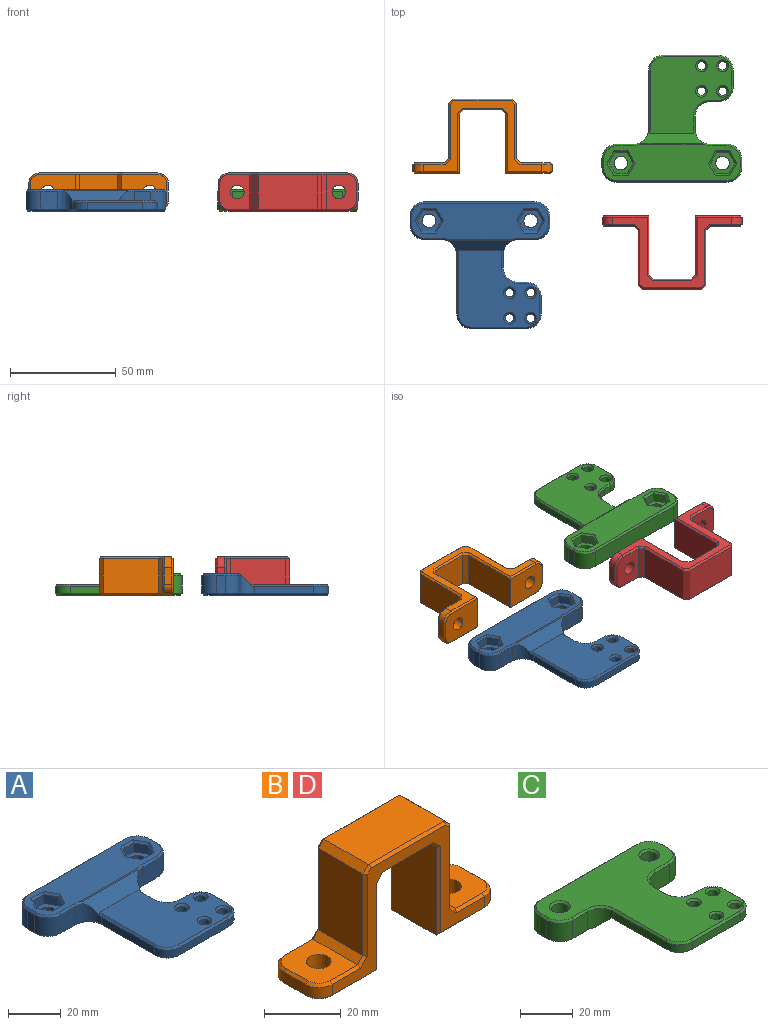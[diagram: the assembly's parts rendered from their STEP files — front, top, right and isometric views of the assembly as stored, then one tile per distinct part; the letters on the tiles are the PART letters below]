
ASSEMBLY  parts=4 mates=3
PART A: 109 faces, bbox 66x60x10 mm
  f0: plane 8.4x8mm, normal (0,-1,0), area 67.2mm2, adj f34,f35,f63,f89
  f1: plane 11.55x10mm, normal (0,0,1), area 54.4mm2, adj f18,f25,f26,f27,f28,f29,f30
  f2: plane 38.66x36.2mm, normal (0,0,1), area 995.8mm2, adj f43,f44,f45,f46,f47,f48,f49,f50
  f3: plane 11.55x10mm, normal (0,0,1), area 54.4mm2, adj f16,f20,f21,f22,f23,f24,f31
  f4: plane 28x3.4mm, normal (-1,0,0), area 95.2mm2, adj f35,f39,f53,f85
  f5: plane 26x3.4mm, normal (0,-1,0), area 88.4mm2, adj f39,f41,f51,f84
  f6: plane 8x3.4mm, normal (1,0,0), area 27.2mm2, adj f41,f42,f49,f88
  f7: plane 4x3.4mm, normal (0,1,0), area 13.6mm2, adj f40,f42,f47,f92
  f8: plane 6x3.4mm, normal (1,0,0), area 20.4mm2, adj f36,f40,f45,f96
  f9: plane 8.4x8mm, normal (0,-1,0), area 67.2mm2, adj f36,f37,f70,f100
  f10: plane 8.4x4mm, normal (1,0,0), area 33.6mm2, adj f37,f38,f66,f101
  f11: plane 52x8.4mm, normal (0,1,0), area 436.8mm2, adj f33,f38,f62,f97
  f12: cylinder r=2mm len=4mm, axis (0,0,1), area 42.7mm2, adj f58,f108
  f13: cylinder r=2mm len=4mm, axis (0,0,1), area 42.7mm2, adj f56,f107
  f14: cylinder r=2mm len=4mm, axis (0,0,1), area 42.7mm2, adj f57,f106
  f15: cylinder r=2mm len=4mm, axis (0,0,1), area 42.7mm2, adj f55,f105
  f16: cylinder r=3.2mm len=6.4mm, axis (0,0,1), area 84.4mm2, adj f3,f103
  f17: plane 8.4x4mm, normal (-1,0,0), area 33.6mm2, adj f33,f34,f59,f93
  f18: cylinder r=3.2mm len=6.4mm, axis (0,0,1), area 84.4mm2, adj f1,f104
  f19: plane 64.4x58.4mm, normal (0,0,-1), area 2062.5mm2, adj f83,f84,f85,f86,f87,f88,f89,f90
  f20: plane 5.77x4.2mm, normal (0,-1,0), area 24.2mm2, adj f3,f21,f31,f75
  f21: plane 5x4.2mm, normal (-0.87,-0.5,0), area 24.2mm2, adj f3,f20,f22,f76
  f22: plane 5x4.2mm, normal (-0.87,0.5,0), area 24.2mm2, adj f3,f21,f23,f74
  f23: plane 5.77x4.2mm, normal (0,1,0), area 24.2mm2, adj f3,f22,f24,f72
  f24: plane 5x4.2mm, normal (0.87,0.5,0), area 24.2mm2, adj f3,f23,f31,f71
  f25: plane 5.77x4.2mm, normal (0,-1,0), area 24.2mm2, adj f1,f26,f30,f81
  f26: plane 5x4.2mm, normal (-0.87,-0.5,0), area 24.2mm2, adj f1,f25,f27,f82
  f27: plane 5x4.2mm, normal (-0.87,0.5,0), area 24.2mm2, adj f1,f26,f28,f80
  f28: plane 5.77x4.2mm, normal (0,1,0), area 24.2mm2, adj f1,f27,f29,f78
  f29: plane 5x4.2mm, normal (0.87,0.5,0), area 24.2mm2, adj f1,f28,f30,f77
  f30: plane 5x4.2mm, normal (0.87,-0.5,0), area 24.2mm2, adj f1,f25,f29,f79
  f31: plane 5x4.2mm, normal (0.87,-0.5,0), area 24.2mm2, adj f3,f20,f24,f73
  f32: plane 64.4x16.87mm, normal (0,0,1), area 805.3mm2, adj f59,f60,f61,f62,f63,f64,f65,f66
  f33: cylinder r=7mm len=8.4mm, axis (0,0,1), area 92.4mm2, adj f11,f17,f60,f95
  f34: cylinder r=7mm len=8.4mm, axis (0,0,1), area 92.4mm2, adj f0,f17,f61,f91
  f35: cylinder r=7mm len=8.4mm, axis (0,0,-1), area 72.1mm2, adj f0,f4,f43,f54,f65,f87
  f36: cylinder r=7mm len=8.4mm, axis (0,0,1), area 72.1mm2, adj f8,f9,f43,f44,f69,f98
  f37: cylinder r=7mm len=8.4mm, axis (0,0,-1), area 92.4mm2, adj f9,f10,f68,f102
  f38: cylinder r=7mm len=8.4mm, axis (0,0,-1), area 92.4mm2, adj f10,f11,f64,f99
  f39: cylinder r=7mm len=7mm, axis (0,0,1), area 37.4mm2, adj f4,f5,f52,f83
  f40: cylinder r=7mm len=7mm, axis (0,0,-1), area 37.4mm2, adj f7,f8,f46,f94
  f41: cylinder r=7mm len=7mm, axis (0,0,1), area 37.4mm2, adj f5,f6,f50,f86
  f42: cylinder r=7mm len=7mm, axis (0,0,-1), area 37.4mm2, adj f6,f7,f48,f90
  f43: plane 29.5x5.57mm, normal (0,-0.71,0.71), area 173.4mm2, adj f2,f35,f36,f44,f54,f65,f67,f69
  f44: cone r=7.8mm half-angle=45deg, axis (0,0,1), area 1.8mm2, adj f2,f36,f43,f45
  f45: plane 6x0.8mm, normal (0.71,0,0.71), area 6.8mm2, adj f2,f8,f44,f46
  f46: cone r=7.8mm half-angle=45deg, axis (0,0,1), area 13.2mm2, adj f2,f40,f45,f47
  f47: plane 4x0.8mm, normal (0,0.71,0.71), area 4.5mm2, adj f2,f7,f46,f48
  f48: cone r=6.2mm half-angle=45deg, axis (0,0,-1), area 11.7mm2, adj f2,f42,f47,f49
  f49: plane 8x0.8mm, normal (0.71,0,0.71), area 9.1mm2, adj f2,f6,f48,f50
  f50: cone r=6.2mm half-angle=45deg, axis (0,0,-1), area 11.7mm2, adj f2,f41,f49,f51
  f51: plane 26x0.8mm, normal (0,-0.71,0.71), area 29.4mm2, adj f2,f5,f50,f52
  f52: cone r=6.2mm half-angle=45deg, axis (0,0,-1), area 11.7mm2, adj f2,f39,f51,f53
  f53: plane 28x0.8mm, normal (-0.71,0,0.71), area 31.7mm2, adj f2,f4,f52,f54
  f54: cone r=7.8mm half-angle=45deg, axis (0,0,1), area 1.8mm2, adj f2,f35,f43,f53
  f55: cone r=2.8mm half-angle=45deg, axis (0,0,1), area 17.1mm2, adj f2,f15
  f56: cone r=2.8mm half-angle=45deg, axis (0,0,1), area 17.1mm2, adj f2,f13
  f57: cone r=2.8mm half-angle=45deg, axis (0,0,1), area 17.1mm2, adj f2,f14
  f58: cone r=2.8mm half-angle=45deg, axis (0,0,1), area 17.1mm2, adj f2,f12
  f59: plane 4x0.8mm, normal (-0.71,0,0.71), area 4.5mm2, adj f17,f32,f60,f61
  f60: cone r=6.2mm half-angle=45deg, axis (0,0,-1), area 11.7mm2, adj f32,f33,f59,f62
  f61: cone r=6.2mm half-angle=45deg, axis (0,0,-1), area 11.7mm2, adj f32,f34,f59,f63
  f62: plane 52x0.8mm, normal (0,0.71,0.71), area 58.8mm2, adj f11,f32,f60,f64
  f63: plane 8x0.8mm, normal (0,-0.71,0.71), area 9.1mm2, adj f0,f32,f61,f65
  f64: cone r=6.2mm half-angle=45deg, axis (0,0,-1), area 11.7mm2, adj f32,f38,f62,f66
  f65: cone r=7.8mm half-angle=45deg, axis (0,0,1), area 3.8mm2, adj f32,f35,f43,f63,f67
  f66: plane 4x0.8mm, normal (0.71,0,0.71), area 4.5mm2, adj f10,f32,f64,f68
  f67: plane 30.67x0.57mm, normal (0,-0.38,0.92), area 18.3mm2, adj f32,f43,f65,f69
  f68: cone r=6.2mm half-angle=45deg, axis (0,0,-1), area 11.7mm2, adj f32,f37,f66,f70
  f69: cone r=7.8mm half-angle=45deg, axis (0,0,1), area 3.8mm2, adj f32,f36,f43,f67,f70
  f70: plane 8x0.8mm, normal (0,-0.71,0.71), area 9.1mm2, adj f9,f32,f68,f69
  f71: plane 5.8x3.81mm, normal (0.61,0.35,0.71), area 7.1mm2, adj f24,f32,f72,f73
  f72: plane 6.7x0.8mm, normal (0,0.71,0.71), area 7.1mm2, adj f23,f32,f71,f74
  f73: plane 5.8x3.81mm, normal (0.61,-0.35,0.71), area 7.1mm2, adj f31,f32,f71,f75
  f74: plane 5.8x3.81mm, normal (-0.61,0.35,0.71), area 7.1mm2, adj f22,f32,f72,f76
  f75: plane 6.7x0.8mm, normal (0,-0.71,0.71), area 7.1mm2, adj f20,f32,f73,f76
  f76: plane 5.8x3.81mm, normal (-0.61,-0.35,0.71), area 7.1mm2, adj f21,f32,f74,f75
  f77: plane 5.8x3.81mm, normal (0.61,0.35,0.71), area 7.1mm2, adj f29,f32,f78,f79
  f78: plane 6.7x0.8mm, normal (0,0.71,0.71), area 7.1mm2, adj f28,f32,f77,f80
  f79: plane 5.8x3.81mm, normal (0.61,-0.35,0.71), area 7.1mm2, adj f30,f32,f77,f81
  f80: plane 5.8x3.81mm, normal (-0.61,0.35,0.71), area 7.1mm2, adj f27,f32,f78,f82
  f81: plane 6.7x0.8mm, normal (0,-0.71,0.71), area 7.1mm2, adj f25,f32,f79,f82
  f82: plane 5.8x3.81mm, normal (-0.61,-0.35,0.71), area 7.1mm2, adj f26,f32,f80,f81
  f83: cone r=6.2mm half-angle=45deg, axis (0,0,1), area 11.7mm2, adj f19,f39,f84,f85
  f84: plane 26x0.8mm, normal (0,-0.71,-0.71), area 29.4mm2, adj f5,f19,f83,f86
  f85: plane 28x0.8mm, normal (-0.71,0,-0.71), area 31.7mm2, adj f4,f19,f83,f87
  f86: cone r=6.2mm half-angle=45deg, axis (0,0,1), area 11.7mm2, adj f19,f41,f84,f88
  f87: cone r=7.8mm half-angle=45deg, axis (0,0,-1), area 13.2mm2, adj f19,f35,f85,f89
  f88: plane 8x0.8mm, normal (0.71,0,-0.71), area 9.1mm2, adj f6,f19,f86,f90
  f89: plane 8x0.8mm, normal (0,-0.71,-0.71), area 9.1mm2, adj f0,f19,f87,f91
  f90: cone r=6.2mm half-angle=45deg, axis (0,0,1), area 11.7mm2, adj f19,f42,f88,f92
  f91: cone r=6.2mm half-angle=45deg, axis (0,0,1), area 11.7mm2, adj f19,f34,f89,f93
  f92: plane 4x0.8mm, normal (0,0.71,-0.71), area 4.5mm2, adj f7,f19,f90,f94
  f93: plane 4x0.8mm, normal (-0.71,0,-0.71), area 4.5mm2, adj f17,f19,f91,f95
  f94: cone r=7.8mm half-angle=45deg, axis (0,0,-1), area 13.2mm2, adj f19,f40,f92,f96
  f95: cone r=6.2mm half-angle=45deg, axis (0,0,1), area 11.7mm2, adj f19,f33,f93,f97
  f96: plane 6x0.8mm, normal (0.71,0,-0.71), area 6.8mm2, adj f8,f19,f94,f98
  f97: plane 52x0.8mm, normal (0,0.71,-0.71), area 58.8mm2, adj f11,f19,f95,f99
  f98: cone r=7.8mm half-angle=45deg, axis (0,0,-1), area 13.2mm2, adj f19,f36,f96,f100
  f99: cone r=6.2mm half-angle=45deg, axis (0,0,1), area 11.7mm2, adj f19,f38,f97,f101
  f100: plane 8x0.8mm, normal (0,-0.71,-0.71), area 9.1mm2, adj f9,f19,f98,f102
  f101: plane 4x0.8mm, normal (0.71,0,-0.71), area 4.5mm2, adj f10,f19,f99,f102
  f102: cone r=6.2mm half-angle=45deg, axis (0,0,1), area 11.7mm2, adj f19,f37,f100,f101
  f103: cone r=3.2mm half-angle=45deg, axis (0,0,-1), area 25.6mm2, adj f16,f19
  f104: cone r=3.2mm half-angle=45deg, axis (0,0,-1), area 25.6mm2, adj f18,f19
  f105: cone r=2mm half-angle=45deg, axis (0,0,-1), area 17.1mm2, adj f15,f19
  f106: cone r=2mm half-angle=45deg, axis (0,0,-1), area 17.1mm2, adj f14,f19
  f107: cone r=2mm half-angle=45deg, axis (0,0,-1), area 17.1mm2, adj f13,f19
  f108: cone r=2mm half-angle=45deg, axis (0,0,-1), area 17.1mm2, adj f12,f19
PART B: 70 faces, bbox 66x18x35 mm
  f0: plane 16.4x14.2mm, normal (0,0,1), area 193.1mm2, adj f5,f21,f26,f27,f28,f29,f30
  f1: plane 56x33.4mm, normal (0,-1,0), area 404.2mm2, adj f16,f18,f30,f32,f34,f36,f38,f40
  f2: plane 28x16.4mm, normal (1,0,0), area 459.2mm2, adj f6,f24,f55,f56
  f3: plane 56x33.4mm, normal (0,1,0), area 404.2mm2, adj f17,f19,f29,f31,f33,f35,f37,f39
  f4: plane 8x3.4mm, normal (-1,0,0), area 27.2mm2, adj f18,f19,f26,f50
  f5: cylinder r=3.2mm len=6.4mm, axis (0,0,1), area 100.5mm2, adj f0,f6
  f6: plane 21.2x16.4mm, normal (0,0,-1), area 307.9mm2, adj f2,f5,f50,f51,f52,f53,f54
  f7: plane 26x16.4mm, normal (-1,0,0), area 426.4mm2, adj f21,f25,f33,f34
  f8: plane 18x16.4mm, normal (0,0,-1), area 295.2mm2, adj f23,f24,f59,f60
  f9: plane 28x16.4mm, normal (-1,0,0), area 459.2mm2, adj f12,f23,f63,f64
  f10: plane 8x3.4mm, normal (1,0,0), area 27.2mm2, adj f16,f17,f49,f69
  f11: cylinder r=3.2mm len=6.4mm, axis (0,0,1), area 100.5mm2, adj f12,f13
  f12: plane 21.2x16.4mm, normal (0,0,-1), area 307.9mm2, adj f9,f11,f65,f66,f67,f68,f69
  f13: plane 16.4x14.2mm, normal (0,0,1), area 193.1mm2, adj f11,f20,f45,f46,f47,f48,f49
  f14: plane 26x16.4mm, normal (1,0,0), area 426.4mm2, adj f20,f22,f41,f42
  f15: plane 28x16.4mm, normal (0,0,1), area 459.2mm2, adj f22,f25,f37,f38
  f16: cylinder r=5mm len=5mm, axis (0,0,1), area 26.7mm2, adj f1,f10,f48,f68
  f17: cylinder r=5mm len=5mm, axis (0,0,-1), area 26.7mm2, adj f3,f10,f47,f67
  f18: cylinder r=5mm len=5mm, axis (0,0,-1), area 26.7mm2, adj f1,f4,f28,f52
  f19: cylinder r=5mm len=5mm, axis (0,0,1), area 26.7mm2, adj f3,f4,f27,f51
  f20: plane 16.4x2mm, normal (0.71,0,0.71), area 46.4mm2, adj f13,f14,f43,f44
  f21: plane 16.4x2mm, normal (-0.71,0,0.71), area 46.4mm2, adj f0,f7,f31,f32
  f22: plane 16.4x2mm, normal (0.71,0,0.71), area 46.4mm2, adj f14,f15,f39,f40
  f23: plane 16.4x2mm, normal (-0.71,0,-0.71), area 46.4mm2, adj f8,f9,f61,f62
  f24: plane 16.4x2mm, normal (0.71,0,-0.71), area 46.4mm2, adj f2,f8,f57,f58
  f25: plane 16.4x2mm, normal (-0.71,0,0.71), area 46.4mm2, adj f7,f15,f35,f36
  f26: plane 8x0.8mm, normal (-0.71,0,0.71), area 9.1mm2, adj f0,f4,f27,f28
  f27: cone r=4.2mm half-angle=45deg, axis (0,0,-1), area 8.2mm2, adj f0,f19,f26,f29
  f28: cone r=4.2mm half-angle=45deg, axis (0,0,-1), area 8.2mm2, adj f0,f18,f26,f30
  f29: plane 10.33x0.8mm, normal (0,0.71,0.71), area 11.5mm2, adj f0,f3,f27,f31
  f30: plane 10.33x0.8mm, normal (0,-0.71,0.71), area 11.5mm2, adj f0,f1,f28,f32
  f31: plane 2.8x2.8mm, normal (-0.5,0.71,0.5), area 3.6mm2, adj f3,f21,f29,f33
  f32: plane 2.8x2.8mm, normal (-0.5,-0.71,0.5), area 3.6mm2, adj f1,f21,f30,f34
  f33: plane 26.33x0.8mm, normal (-0.71,0.71,0), area 29.4mm2, adj f3,f7,f31,f35
  f34: plane 26.33x0.8mm, normal (-0.71,-0.71,0), area 29.4mm2, adj f1,f7,f32,f36
  f35: plane 2.33x2.33mm, normal (-0.5,0.71,0.5), area 2.8mm2, adj f3,f25,f33,f37
  f36: plane 2.33x2.33mm, normal (-0.5,-0.71,0.5), area 2.8mm2, adj f1,f25,f34,f38
  f37: plane 28x0.8mm, normal (0,0.71,0.71), area 31.3mm2, adj f3,f15,f35,f39
  f38: plane 28x0.8mm, normal (0,-0.71,0.71), area 31.3mm2, adj f1,f15,f36,f40
  f39: plane 2.33x2.33mm, normal (0.5,0.71,0.5), area 2.8mm2, adj f3,f22,f37,f41
  f40: plane 2.33x2.33mm, normal (0.5,-0.71,0.5), area 2.8mm2, adj f1,f22,f38,f42
  f41: plane 26.33x0.8mm, normal (0.71,0.71,0), area 29.4mm2, adj f3,f14,f39,f43
  f42: plane 26.33x0.8mm, normal (0.71,-0.71,0), area 29.4mm2, adj f1,f14,f40,f44
  f43: plane 2.8x2.8mm, normal (0.5,0.71,0.5), area 3.6mm2, adj f3,f20,f41,f45
  f44: plane 2.8x2.8mm, normal (0.5,-0.71,0.5), area 3.6mm2, adj f1,f20,f42,f46
  f45: plane 10.33x0.8mm, normal (0,0.71,0.71), area 11.5mm2, adj f3,f13,f43,f47
  f46: plane 10.33x0.8mm, normal (0,-0.71,0.71), area 11.5mm2, adj f1,f13,f44,f48
  f47: cone r=4.2mm half-angle=45deg, axis (0,0,-1), area 8.2mm2, adj f13,f17,f45,f49
  f48: cone r=4.2mm half-angle=45deg, axis (0,0,-1), area 8.2mm2, adj f13,f16,f46,f49
  f49: plane 8x0.8mm, normal (0.71,0,0.71), area 9.1mm2, adj f10,f13,f47,f48
  f50: plane 8x0.8mm, normal (-0.71,0,-0.71), area 9.1mm2, adj f4,f6,f51,f52
  f51: cone r=4.2mm half-angle=45deg, axis (0,0,1), area 8.2mm2, adj f6,f19,f50,f53
  f52: cone r=4.2mm half-angle=45deg, axis (0,0,1), area 8.2mm2, adj f6,f18,f50,f54
  f53: plane 17x0.8mm, normal (0,0.71,-0.71), area 18.8mm2, adj f3,f6,f51,f55
  f54: plane 17x0.8mm, normal (0,-0.71,-0.71), area 18.8mm2, adj f1,f6,f52,f56
  f55: plane 28.33x0.8mm, normal (0.71,0.71,0), area 31.4mm2, adj f2,f3,f53,f57
  f56: plane 28.33x0.8mm, normal (0.71,-0.71,0), area 31.4mm2, adj f1,f2,f54,f58
  f57: plane 2.8x2.8mm, normal (0.5,0.71,-0.5), area 3.6mm2, adj f3,f24,f55,f59
  f58: plane 2.8x2.8mm, normal (0.5,-0.71,-0.5), area 3.6mm2, adj f1,f24,f56,f60
  f59: plane 18.66x0.8mm, normal (0,0.71,-0.71), area 20.7mm2, adj f3,f8,f57,f61
  f60: plane 18.66x0.8mm, normal (0,-0.71,-0.71), area 20.7mm2, adj f1,f8,f58,f62
  f61: plane 2.8x2.8mm, normal (-0.5,0.71,-0.5), area 3.6mm2, adj f3,f23,f59,f63
  f62: plane 2.8x2.8mm, normal (-0.5,-0.71,-0.5), area 3.6mm2, adj f1,f23,f60,f64
  f63: plane 28.33x0.8mm, normal (-0.71,0.71,0), area 31.4mm2, adj f3,f9,f61,f65
  f64: plane 28.33x0.8mm, normal (-0.71,-0.71,0), area 31.4mm2, adj f1,f9,f62,f66
  f65: plane 17x0.8mm, normal (0,0.71,-0.71), area 18.8mm2, adj f3,f12,f63,f67
  f66: plane 17x0.8mm, normal (0,-0.71,-0.71), area 18.8mm2, adj f1,f12,f64,f68
  f67: cone r=4.2mm half-angle=45deg, axis (0,0,1), area 8.2mm2, adj f12,f17,f65,f69
  f68: cone r=4.2mm half-angle=45deg, axis (0,0,1), area 8.2mm2, adj f12,f16,f66,f69
  f69: plane 8x0.8mm, normal (0.71,0,-0.71), area 9.1mm2, adj f10,f12,f67,f68
PART C: 109 faces, bbox 66x60x10 mm
  f0: plane 8.4x8mm, normal (0,-1,0), area 67.2mm2, adj f34,f35,f63,f89
  f1: plane 11.55x10mm, normal (0,0,-1), area 54.4mm2, adj f18,f25,f26,f27,f28,f29,f30
  f2: plane 38.66x36.2mm, normal (0,0,-1), area 995.8mm2, adj f43,f44,f45,f46,f47,f48,f49,f50
  f3: plane 11.55x10mm, normal (0,0,-1), area 54.4mm2, adj f16,f20,f21,f22,f23,f24,f31
  f4: plane 28x3.4mm, normal (-1,0,0), area 95.2mm2, adj f35,f39,f53,f85
  f5: plane 26x3.4mm, normal (0,-1,0), area 88.4mm2, adj f39,f41,f51,f84
  f6: plane 8x3.4mm, normal (1,0,0), area 27.2mm2, adj f41,f42,f49,f88
  f7: plane 4x3.4mm, normal (0,1,0), area 13.6mm2, adj f40,f42,f47,f92
  f8: plane 6x3.4mm, normal (1,0,0), area 20.4mm2, adj f36,f40,f45,f96
  f9: plane 8.4x8mm, normal (0,-1,0), area 67.2mm2, adj f36,f37,f70,f100
  f10: plane 8.4x4mm, normal (1,0,0), area 33.6mm2, adj f37,f38,f66,f101
  f11: plane 52x8.4mm, normal (0,1,0), area 436.8mm2, adj f33,f38,f62,f97
  f12: cylinder r=2mm len=4mm, axis (0,0,-1), area 42.7mm2, adj f58,f108
  f13: cylinder r=2mm len=4mm, axis (0,0,-1), area 42.7mm2, adj f56,f107
  f14: cylinder r=2mm len=4mm, axis (0,0,-1), area 42.7mm2, adj f57,f106
  f15: cylinder r=2mm len=4mm, axis (0,0,-1), area 42.7mm2, adj f55,f105
  f16: cylinder r=3.2mm len=6.4mm, axis (0,0,-1), area 84.4mm2, adj f3,f103
  f17: plane 8.4x4mm, normal (-1,0,0), area 33.6mm2, adj f33,f34,f59,f93
  f18: cylinder r=3.2mm len=6.4mm, axis (0,0,-1), area 84.4mm2, adj f1,f104
  f19: plane 64.4x58.4mm, normal (0,0,1), area 2062.5mm2, adj f83,f84,f85,f86,f87,f88,f89,f90
  f20: plane 5.77x4.2mm, normal (0,-1,0), area 24.2mm2, adj f3,f21,f31,f75
  f21: plane 5x4.2mm, normal (-0.87,-0.5,0), area 24.2mm2, adj f3,f20,f22,f76
  f22: plane 5x4.2mm, normal (-0.87,0.5,0), area 24.2mm2, adj f3,f21,f23,f74
  f23: plane 5.77x4.2mm, normal (0,1,0), area 24.2mm2, adj f3,f22,f24,f72
  f24: plane 5x4.2mm, normal (0.87,0.5,0), area 24.2mm2, adj f3,f23,f31,f71
  f25: plane 5.77x4.2mm, normal (0,-1,0), area 24.2mm2, adj f1,f26,f30,f81
  f26: plane 5x4.2mm, normal (-0.87,-0.5,0), area 24.2mm2, adj f1,f25,f27,f82
  f27: plane 5x4.2mm, normal (-0.87,0.5,0), area 24.2mm2, adj f1,f26,f28,f80
  f28: plane 5.77x4.2mm, normal (0,1,0), area 24.2mm2, adj f1,f27,f29,f78
  f29: plane 5x4.2mm, normal (0.87,0.5,0), area 24.2mm2, adj f1,f28,f30,f77
  f30: plane 5x4.2mm, normal (0.87,-0.5,0), area 24.2mm2, adj f1,f25,f29,f79
  f31: plane 5x4.2mm, normal (0.87,-0.5,0), area 24.2mm2, adj f3,f20,f24,f73
  f32: plane 64.4x16.87mm, normal (0,0,-1), area 805.3mm2, adj f59,f60,f61,f62,f63,f64,f65,f66
  f33: cylinder r=7mm len=8.4mm, axis (0,0,-1), area 92.4mm2, adj f11,f17,f60,f95
  f34: cylinder r=7mm len=8.4mm, axis (0,0,-1), area 92.4mm2, adj f0,f17,f61,f91
  f35: cylinder r=7mm len=8.4mm, axis (0,0,1), area 72.1mm2, adj f0,f4,f43,f54,f65,f87
  f36: cylinder r=7mm len=8.4mm, axis (0,0,-1), area 72.1mm2, adj f8,f9,f43,f44,f69,f98
  f37: cylinder r=7mm len=8.4mm, axis (0,0,1), area 92.4mm2, adj f9,f10,f68,f102
  f38: cylinder r=7mm len=8.4mm, axis (0,0,1), area 92.4mm2, adj f10,f11,f64,f99
  f39: cylinder r=7mm len=7mm, axis (0,0,-1), area 37.4mm2, adj f4,f5,f52,f83
  f40: cylinder r=7mm len=7mm, axis (0,0,1), area 37.4mm2, adj f7,f8,f46,f94
  f41: cylinder r=7mm len=7mm, axis (0,0,-1), area 37.4mm2, adj f5,f6,f50,f86
  f42: cylinder r=7mm len=7mm, axis (0,0,1), area 37.4mm2, adj f6,f7,f48,f90
  f43: plane 29.5x5.57mm, normal (0,-0.71,-0.71), area 173.4mm2, adj f2,f35,f36,f44,f54,f65,f67,f69
  f44: cone r=7.8mm half-angle=45deg, axis (0,0,-1), area 1.8mm2, adj f2,f36,f43,f45
  f45: plane 6x0.8mm, normal (0.71,0,-0.71), area 6.8mm2, adj f2,f8,f44,f46
  f46: cone r=7.8mm half-angle=45deg, axis (0,0,-1), area 13.2mm2, adj f2,f40,f45,f47
  f47: plane 4x0.8mm, normal (0,0.71,-0.71), area 4.5mm2, adj f2,f7,f46,f48
  f48: cone r=6.2mm half-angle=45deg, axis (0,0,1), area 11.7mm2, adj f2,f42,f47,f49
  f49: plane 8x0.8mm, normal (0.71,0,-0.71), area 9.1mm2, adj f2,f6,f48,f50
  f50: cone r=6.2mm half-angle=45deg, axis (0,0,1), area 11.7mm2, adj f2,f41,f49,f51
  f51: plane 26x0.8mm, normal (0,-0.71,-0.71), area 29.4mm2, adj f2,f5,f50,f52
  f52: cone r=6.2mm half-angle=45deg, axis (0,0,1), area 11.7mm2, adj f2,f39,f51,f53
  f53: plane 28x0.8mm, normal (-0.71,0,-0.71), area 31.7mm2, adj f2,f4,f52,f54
  f54: cone r=7.8mm half-angle=45deg, axis (0,0,-1), area 1.8mm2, adj f2,f35,f43,f53
  f55: cone r=2.8mm half-angle=45deg, axis (0,0,-1), area 17.1mm2, adj f2,f15
  f56: cone r=2.8mm half-angle=45deg, axis (0,0,-1), area 17.1mm2, adj f2,f13
  f57: cone r=2.8mm half-angle=45deg, axis (0,0,-1), area 17.1mm2, adj f2,f14
  f58: cone r=2.8mm half-angle=45deg, axis (0,0,-1), area 17.1mm2, adj f2,f12
  f59: plane 4x0.8mm, normal (-0.71,0,-0.71), area 4.5mm2, adj f17,f32,f60,f61
  f60: cone r=6.2mm half-angle=45deg, axis (0,0,1), area 11.7mm2, adj f32,f33,f59,f62
  f61: cone r=6.2mm half-angle=45deg, axis (0,0,1), area 11.7mm2, adj f32,f34,f59,f63
  f62: plane 52x0.8mm, normal (0,0.71,-0.71), area 58.8mm2, adj f11,f32,f60,f64
  f63: plane 8x0.8mm, normal (0,-0.71,-0.71), area 9.1mm2, adj f0,f32,f61,f65
  f64: cone r=6.2mm half-angle=45deg, axis (0,0,1), area 11.7mm2, adj f32,f38,f62,f66
  f65: cone r=7.8mm half-angle=45deg, axis (0,0,-1), area 3.8mm2, adj f32,f35,f43,f63,f67
  f66: plane 4x0.8mm, normal (0.71,0,-0.71), area 4.5mm2, adj f10,f32,f64,f68
  f67: plane 30.67x0.57mm, normal (0,-0.38,-0.92), area 18.3mm2, adj f32,f43,f65,f69
  f68: cone r=6.2mm half-angle=45deg, axis (0,0,1), area 11.7mm2, adj f32,f37,f66,f70
  f69: cone r=7.8mm half-angle=45deg, axis (0,0,-1), area 3.8mm2, adj f32,f36,f43,f67,f70
  f70: plane 8x0.8mm, normal (0,-0.71,-0.71), area 9.1mm2, adj f9,f32,f68,f69
  f71: plane 5.8x3.81mm, normal (0.61,0.35,-0.71), area 7.1mm2, adj f24,f32,f72,f73
  f72: plane 6.7x0.8mm, normal (0,0.71,-0.71), area 7.1mm2, adj f23,f32,f71,f74
  f73: plane 5.8x3.81mm, normal (0.61,-0.35,-0.71), area 7.1mm2, adj f31,f32,f71,f75
  f74: plane 5.8x3.81mm, normal (-0.61,0.35,-0.71), area 7.1mm2, adj f22,f32,f72,f76
  f75: plane 6.7x0.8mm, normal (0,-0.71,-0.71), area 7.1mm2, adj f20,f32,f73,f76
  f76: plane 5.8x3.81mm, normal (-0.61,-0.35,-0.71), area 7.1mm2, adj f21,f32,f74,f75
  f77: plane 5.8x3.81mm, normal (0.61,0.35,-0.71), area 7.1mm2, adj f29,f32,f78,f79
  f78: plane 6.7x0.8mm, normal (0,0.71,-0.71), area 7.1mm2, adj f28,f32,f77,f80
  f79: plane 5.8x3.81mm, normal (0.61,-0.35,-0.71), area 7.1mm2, adj f30,f32,f77,f81
  f80: plane 5.8x3.81mm, normal (-0.61,0.35,-0.71), area 7.1mm2, adj f27,f32,f78,f82
  f81: plane 6.7x0.8mm, normal (0,-0.71,-0.71), area 7.1mm2, adj f25,f32,f79,f82
  f82: plane 5.8x3.81mm, normal (-0.61,-0.35,-0.71), area 7.1mm2, adj f26,f32,f80,f81
  f83: cone r=6.2mm half-angle=45deg, axis (0,0,-1), area 11.7mm2, adj f19,f39,f84,f85
  f84: plane 26x0.8mm, normal (0,-0.71,0.71), area 29.4mm2, adj f5,f19,f83,f86
  f85: plane 28x0.8mm, normal (-0.71,0,0.71), area 31.7mm2, adj f4,f19,f83,f87
  f86: cone r=6.2mm half-angle=45deg, axis (0,0,-1), area 11.7mm2, adj f19,f41,f84,f88
  f87: cone r=7.8mm half-angle=45deg, axis (0,0,1), area 13.2mm2, adj f19,f35,f85,f89
  f88: plane 8x0.8mm, normal (0.71,0,0.71), area 9.1mm2, adj f6,f19,f86,f90
  f89: plane 8x0.8mm, normal (0,-0.71,0.71), area 9.1mm2, adj f0,f19,f87,f91
  f90: cone r=6.2mm half-angle=45deg, axis (0,0,-1), area 11.7mm2, adj f19,f42,f88,f92
  f91: cone r=6.2mm half-angle=45deg, axis (0,0,-1), area 11.7mm2, adj f19,f34,f89,f93
  f92: plane 4x0.8mm, normal (0,0.71,0.71), area 4.5mm2, adj f7,f19,f90,f94
  f93: plane 4x0.8mm, normal (-0.71,0,0.71), area 4.5mm2, adj f17,f19,f91,f95
  f94: cone r=7.8mm half-angle=45deg, axis (0,0,1), area 13.2mm2, adj f19,f40,f92,f96
  f95: cone r=6.2mm half-angle=45deg, axis (0,0,-1), area 11.7mm2, adj f19,f33,f93,f97
  f96: plane 6x0.8mm, normal (0.71,0,0.71), area 6.8mm2, adj f8,f19,f94,f98
  f97: plane 52x0.8mm, normal (0,0.71,0.71), area 58.8mm2, adj f11,f19,f95,f99
  f98: cone r=7.8mm half-angle=45deg, axis (0,0,1), area 13.2mm2, adj f19,f36,f96,f100
  f99: cone r=6.2mm half-angle=45deg, axis (0,0,-1), area 11.7mm2, adj f19,f38,f97,f101
  f100: plane 8x0.8mm, normal (0,-0.71,0.71), area 9.1mm2, adj f9,f19,f98,f102
  f101: plane 4x0.8mm, normal (0.71,0,0.71), area 4.5mm2, adj f10,f19,f99,f102
  f102: cone r=6.2mm half-angle=45deg, axis (0,0,-1), area 11.7mm2, adj f19,f37,f100,f101
  f103: cone r=3.2mm half-angle=45deg, axis (0,0,1), area 25.6mm2, adj f16,f19
  f104: cone r=3.2mm half-angle=45deg, axis (0,0,1), area 25.6mm2, adj f18,f19
  f105: cone r=2mm half-angle=45deg, axis (0,0,1), area 17.1mm2, adj f15,f19
  f106: cone r=2mm half-angle=45deg, axis (0,0,1), area 17.1mm2, adj f14,f19
  f107: cone r=2mm half-angle=45deg, axis (0,0,1), area 17.1mm2, adj f13,f19
  f108: cone r=2mm half-angle=45deg, axis (0,0,1), area 17.1mm2, adj f12,f19
PART D: same geometry as B
PLACE A t=(-46.47,-34.28,59.87)mm
PLACE B rot(axis=(-1,0,0),90deg) t=(-45.2,-10.88,34.87)mm
PLACE C rot(axis=(1,0,0),180deg) t=(44.16,34.88,9.87)mm
PLACE D rot(axis=(0,-0.71,0.71),180deg) t=(44.3,9.18,34.87)mm
MATE planar A.f19 <-> D.f3  axis (0,0,-1) through (-44.06,-30.41,4.87)mm
MATE planar C.f19 <-> B.f3  axis (0,0,-1) through (46.57,31.01,4.87)mm
MATE planar C.f16 <-> A.f19  axis (0,0,-1) through (68.16,13.88,4.87)mm
